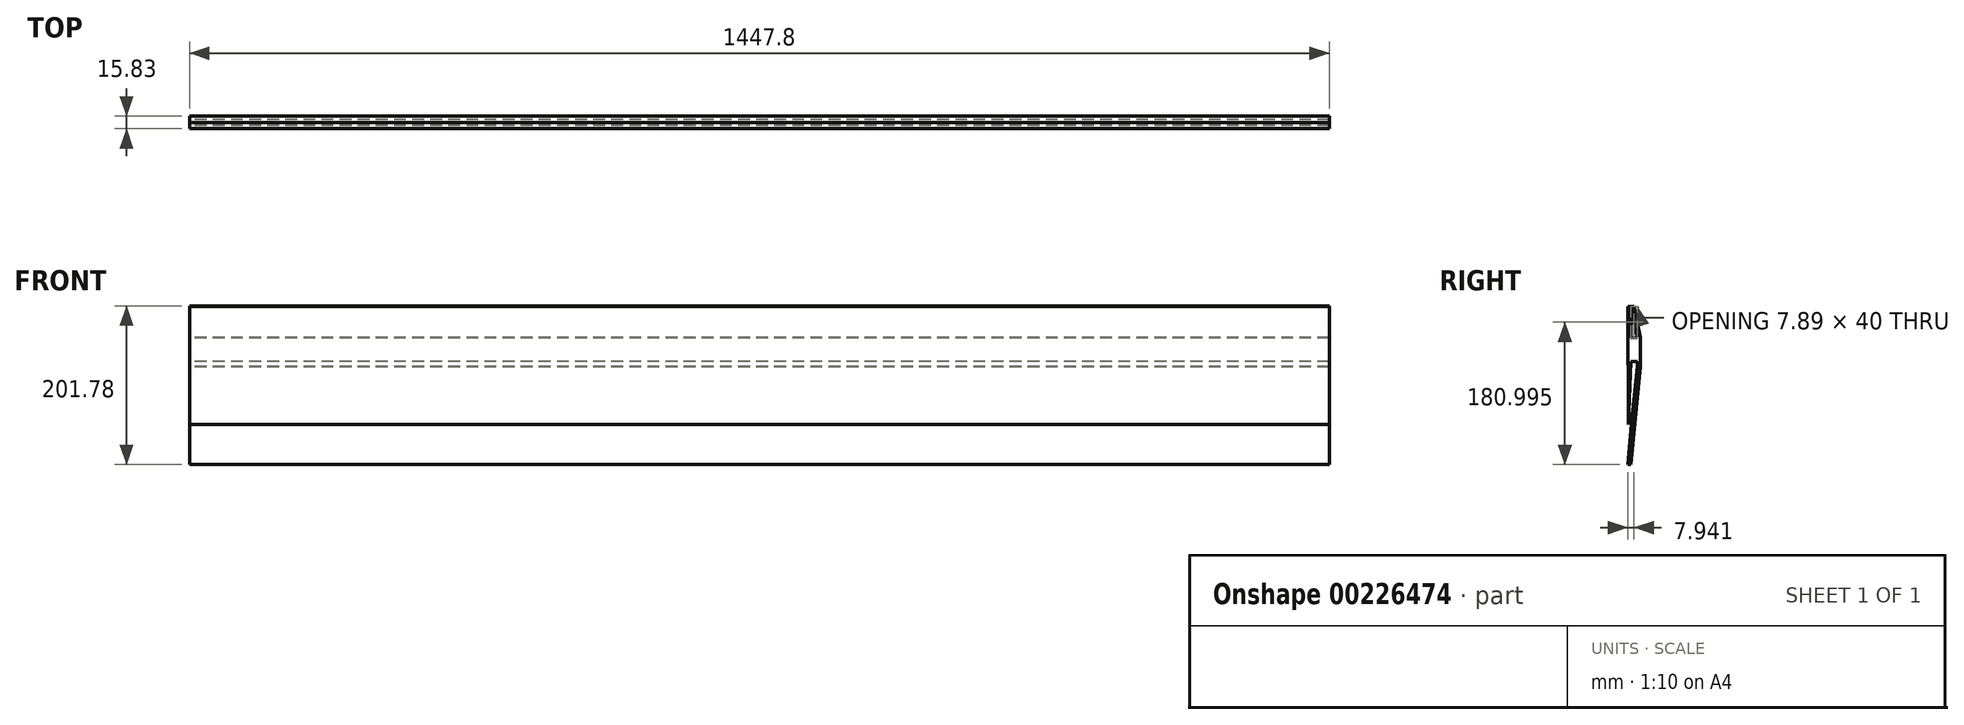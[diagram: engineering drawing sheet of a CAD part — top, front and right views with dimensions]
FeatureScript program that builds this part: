
annotation { "Feature Type Name" : "Feature", "Feature Type Description" : "" }
export const myFeature = defineFeature(function(context is Context, id is Id, definition is map)
    precondition{}
    {
        {
            var Q0;
            Q0=qCreatedBy(makeId("Right.planeOp"),FACE);
            var sketch = newSketch(context, id + "F0", { "sketchPlane" : qUnion([Q0])});
            skPoint(sketch, "E0.1", {"position": v(-11.89, -143.03) * mm});
            skPoint(sketch, "E0.2", {"position": v(-15.83, -142.6) * mm});
            skPoint(sketch, "E0.3", {"position": v(-10.97, -91.82) * mm});
            skPoint(sketch, "E0.4", {"position": v(-14.94, -92.03) * mm});
            skPoint(sketch, "E0.5", {"position": v(-3.94, -12.03) * mm});
            skPoint(sketch, "E0.6", {"position": v(-3.94, -18.53) * mm});
            skPoint(sketch, "E0.7", {"position": v(-11.84, -12.03) * mm});
            skPoint(sketch, "E0.8", {"position": v(0, -18.75) * mm});
            skPoint(sketch, "E0.9", {"position": v(0, 18.75) * mm});
            skPoint(sketch, "E0.10", {"position": v(-3.94, 18.35) * mm});
            skPoint(sketch, "E0.11", {"position": v(-11.84, 17.97) * mm});
            skPoint(sketch, "E1.0", {"position": v(-7.95, 58.75) * mm});
            skPoint(sketch, "E2.0", {"position": v(-11.84, 57.97) * mm});
            skPoint(sketch, "E3.0", {"position": v(-15.82, 57.97) * mm});
            skLineSegment(sketch, "E4", {"start": v(-11.89, -143.03) * mm, "end": v(0, -18.75) * mm});
            skLineSegment(sketch, "E5", {"start": v(0, 18.75) * mm, "end": v(-7.95, 58.75) * mm});
            skLineSegment(sketch, "E6", {"start": v(0, 18.75) * mm, "end": v(0, -18.75) * mm});
            skCircle(sketch, "E7", {"center": v(-11.84, 57.97) * mm, "radius": 3.96 * mm});
            skLineSegment(sketch, "E8", {"start": v(-15.82, 57.97) * mm, "end": v(-14.94, -92.03) * mm});
            skLineSegment(sketch, "E9", {"start": v(-11.84, -12.03) * mm, "end": v(-14.94, -92.03) * mm});
            skLineSegment(sketch, "E10", {"start": v(-3.94, -12.03) * mm, "end": v(-11.84, -12.03) * mm});
            skLineSegment(sketch, "E11", {"start": v(-3.94, -12.03) * mm, "end": v(-3.94, -18.53) * mm});
            skLineSegment(sketch, "E12", {"start": v(-3.94, -18.53) * mm, "end": v(-10.97, -91.82) * mm});
            skLineSegment(sketch, "E13", {"start": v(-10.97, -91.82) * mm, "end": v(-14.94, -92.03) * mm});
            skLineSegment(sketch, "E14", {"start": v(-15.83, -142.6) * mm, "end": v(-11.89, -143.03) * mm});
            skLineSegment(sketch, "E15", {"start": v(-15.83, -142.6) * mm, "end": v(-10.97, -91.82) * mm});
            skLineSegment(sketch, "E16", {"start": v(-3.94, 18.35) * mm, "end": v(-11.84, 57.97) * mm});
            skLineSegment(sketch, "E17", {"start": v(-11.84, 17.97) * mm, "end": v(-11.84, 57.97) * mm});
            skLineSegment(sketch, "E18", {"start": v(-3.94, 18.35) * mm, "end": v(-11.84, 17.97) * mm});
            skLineSegment(sketch, "E19", {"start": v(-7.95, 58.75) * mm, "end": v(-15.82, 57.97) * mm});
            skSolve(sketch);
        }
        {
            var Q0;
            Q0=makeQuery(id+"F0.imprint","IMPRINT",FACE,{"disambiguationData":[TD([[makeQuery(id+"F0.imprint","IMPRINT",EDGE,{"derivedFrom":sQuery(id+"F0.wireOp",EDGE,"E4")}),1.0]])]});
            var Q1;
            {var subQ0=sQuery(id+"F0.wireOp",EDGE,"E19");var subQ1=sQuery(id+"F0.wireOp",EDGE,"E7");var subQ2=makeQuery(id+"F0.imprint","INTERSECT",VERTEX,{"disambiguationData":[OD(0.0)],"derivedFrom":[subQ1,subQ0]});Q1=makeQuery(id+"F0.imprint","IMPRINT",FACE,{"disambiguationData":[TD([[makeQuery(id+"F0.imprint","IMPRINT",EDGE,{"disambiguationData":[TD([[subQ2,-1.0]])],"derivedFrom":subQ1}),1.0]])]});}
            var Q2;
            {var subQ0=sQuery(id+"F0.wireOp",EDGE,"E7");var subQ1=makeQuery(id+"F0.imprint","INTERSECT",VERTEX,{"derivedFrom":[sQuery(id+"F0.wireOp",EDGE,"E5"),subQ0]});Q2=makeQuery(id+"F0.imprint","IMPRINT",FACE,{"disambiguationData":[TD([[makeQuery(id+"F0.imprint","IMPRINT",EDGE,{"disambiguationData":[TD([[subQ1,-1.0]])],"derivedFrom":subQ0}),1.0]])]});}
            extrude(context, id + "F1", {"entities" : qUnion([Q0, Q1, Q2]), "depth" : 1447.8 * mm, "symmetric" : true});
        }
        {
            var Q0;
            Q0=makeQuery(id+"F1.opExtrude","SWEPT_FACE",FACE,{"disambiguationData":[OSD([sQuery(id+"F0.wireOp",EDGE,"E6")])]});
            var sketch = newSketch(context, id + "F2", { "sketchPlane" : qUnion([Q0])});
            skLineSegment(sketch, "E20.bottom", {"start": v(-25.4, -79.53) * mm, "end": v(25.4, -79.53) * mm});
            skLineSegment(sketch, "E20.top", {"start": v(-25.4, -104.93) * mm, "end": v(25.4, -104.93) * mm});
            skLineSegment(sketch, "E20.left", {"start": v(-25.4, -79.53) * mm, "end": v(-25.4, -104.93) * mm});
            skLineSegment(sketch, "E20.right", {"start": v(25.4, -79.53) * mm, "end": v(25.4, -104.93) * mm});
            skLineSegment(sketch, "E21.bottom", {"start": v(-33.66, -104.93) * mm, "end": v(33.66, -104.93) * mm});
            skLineSegment(sketch, "E21.top", {"start": v(-33.66, -143.03) * mm, "end": v(33.66, -143.03) * mm});
            skLineSegment(sketch, "E21.left", {"start": v(-33.66, -104.93) * mm, "end": v(-33.66, -143.03) * mm});
            skLineSegment(sketch, "E21.right", {"start": v(33.65, -104.93) * mm, "end": v(33.66, -143.03) * mm});
            skLineSegment(sketch, "E22", {"start": v(33.66, -104.93) * mm, "end": v(25.4, -104.93) * mm});
            skLineSegment(sketch, "E23", {"start": v(-25.4, -104.93) * mm, "end": v(-33.66, -104.93) * mm});
            skSolve(sketch);
        }
    });
